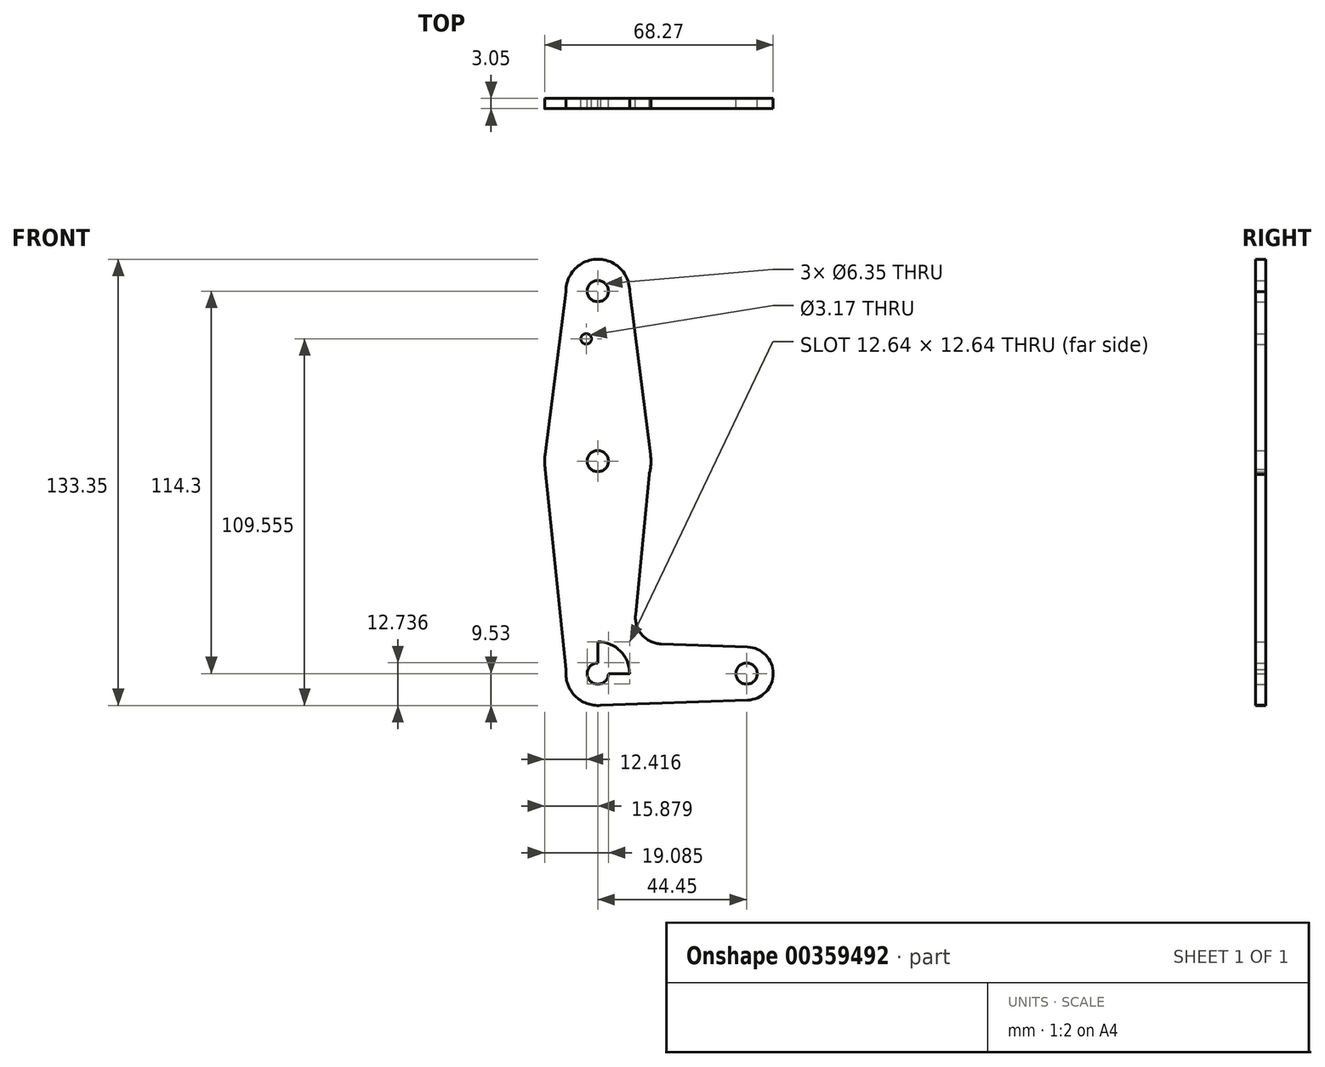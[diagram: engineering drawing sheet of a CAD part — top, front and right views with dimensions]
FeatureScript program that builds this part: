
annotation { "Feature Type Name" : "Feature", "Feature Type Description" : "" }
export const myFeature = defineFeature(function(context is Context, id is Id, definition is map)
    precondition{}
    {
        {
            var Q0;
            Q0=qCreatedBy(makeId("Front.planeOp"),FACE);
            var sketch = newSketch(context, id + "F0", { "sketchPlane" : qUnion([Q0])});
            skCircle(sketch, "E0", {"center": v(-29.93, 50.8) * mm, "radius": 9.53 * mm});
            skCircle(sketch, "E1", {"center": v(-29.93, 0) * mm, "radius": 15.88 * mm});
            skCircle(sketch, "E2", {"center": v(-29.93, -63.5) * mm, "radius": 9.53 * mm});
            skCircle(sketch, "E3", {"center": v(14.52, -63.5) * mm, "radius": 7.94 * mm});
            skLineSegment(sketch, "E4", {"start": v(-29.93, 50.8) * mm, "end": v(-29.93, -63.5) * mm});
            skLineSegment(sketch, "E5", {"start": v(-29.93, -63.5) * mm, "end": v(14.52, -63.5) * mm});
            skCircle(sketch, "E6", {"center": v(-29.93, 50.8) * mm, "radius": 3.18 * mm});
            skLineSegment(sketch, "E7", {"start": v(-39.45, 50.67) * mm, "end": v(-45.93, 0) * mm});
            skLineSegment(sketch, "E8", {"start": v(-45.62, -2.4) * mm, "end": v(-39.38, -62.28) * mm});
            skLineSegment(sketch, "E9", {"start": v(-30.13, -73.02) * mm, "end": v(14.8, -71.43) * mm});
            skLineSegment(sketch, "E10", {"start": v(-20.4, 50.68) * mm, "end": v(-14.18, 2.01) * mm});
            skLineSegment(sketch, "E11", {"start": v(-14.18, 0) * mm, "end": v(-18.65, -45.93) * mm});
            skLineSegment(sketch, "E12", {"start": v(-11.02, -54.65) * mm, "end": v(14.8, -55.57) * mm});
            skCircle(sketch, "E13", {"center": v(-29.93, 0) * mm, "radius": 3.18 * mm});
            skCircle(sketch, "E14", {"center": v(-33.4, 36.53) * mm, "radius": 1.59 * mm});
            skCircle(sketch, "E15", {"center": v(-29.93, -63.5) * mm, "radius": 3.18 * mm});
            skCircle(sketch, "E16", {"center": v(14.52, -63.5) * mm, "radius": 3.18 * mm});
            skArc(sketch, "E17.filletArc", {"start": v(-18.65, -45.93) * mm, "mid": v(-16.72, -51.94) * mm, "end": v(-11.02, -54.65) * mm});
            skSolve(sketch);
        }
        {
            var Q0;
            Q0 = qSketchRegion(id + "F0", true);
            extrude(context, id + "F1", {"entities" : qUnion([Q0]), "depth" : 3.05 * mm});
        }
    });
